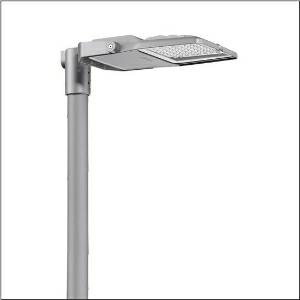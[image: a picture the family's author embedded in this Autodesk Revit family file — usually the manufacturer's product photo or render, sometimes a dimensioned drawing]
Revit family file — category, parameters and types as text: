
# Revit family: floodlight_fl_21_iq_mini___pl33t_5xa7772d2f3a_d038
name_source: partatom
category: Lighting Fixtures
units: mm (PartAtom-declared; Revit-internal decimal feet)

## family parameters
Cut with Voids When Loaded = No
Host = Face
Light Source = No
Part Type = Normal
Room Calculation Point = No
Round Connector Dimension = Use Diameter
Shared = No

## types (1)
- --- (1 x LED, 17620 lm, 143 W, 3000K)
    Apparent Load = 143 VA
    CIE Flux Codes = 26 75 99 100 100
    Color Rendering = 70
    Color Temperature = 3000K
    Default Elevation = 1800 mm
    Description = Floodlight FL 21 iQ mini, floodlight, primary light control with lens, of PMMA, primary optical cover: protective disc, of toughened safety glass, transparent, light distribution: PL33T, light emission: direct distribution, installation type: surface-mounted, lamps: LED, High Power LED, rated values: 17.620lm | 143W | 123,2lm/W (begin service life); end service life: 17.620lm | 151,6W; at 50% lumin. flux: 8.810lm | 60,6W | 145,4lm/W, colour temperature: 3000K, colour rendering: CRI > 70, light colour: 730, light setting 1 begin service life: 100% | 17.620lm | 143W | 123,2lm/W | 3.000K, light setting 1 end service life: 151,6W, further light settings possible, control: pre-setting: linear dimming characteristic, Auto-Match, Temp-Guard, Night-Set, Smart-Wire, Desk-Remote (wireless, voltage-free reading and setting of iQ features in the workshop via application-optimized NFC function/RFID function), optimised constant luminous flux control (CLO 2.0), Light-Fading, Lumen-Switch, with terminal, 6-pole, mains connection: 220..240V, AC, 50/60Hz, luminaire housing, of diecast aluminium, powder-coated, SITECO metallic grey (DB 702S), corrosivity category C5 mid according to DIN EN ISO 12944suitable for swimming poolschlorine-resistant, sealing non-destructively replaceable, please order mast flange separately, mast bracket, of steel, galvanised, powder-coated, protection rating (complete): IP66, insulation class (complete): insulation class II (safety insulation), certification: CE, ENEC, VDE, protection symbol: D, impact resistance: IK08, permissible operating ambient temperature: -40..+40°C, permissible operating ambient temperature for outdoor applications: -40..+50°C, standard: DIN EN 12944, LABS conformity tested according to VDMA 24364:2018-05, packaging unit: 1 piece

Light Distribution: PL33T
    Height = 70 mm
    Lamp = 1 x LED
    Lamp Light Flux = 17620 lm
    Lamp Power = 143 W
    Lamp count = 1
    Length = 485 mm
    Luminous efficacy = 123 lm/W
    Manufacturer = Siteco
    ModVariant = No
    Model = 5XA7772D2F3A
    Number of Poles = 1
    OnlyDefault = Yes
    Power Factor = 1
    Product Name = Floodlight FL 21 iQ mini | PL33T
    Product group = floodlight | pylon annexe
    ProductGroupID = 6201
    Protection Class = Protection class II
    Protection Degree = IP 66
    RLX_Detail_Level = 1
    RLX_Emergency_Light_Flux = 0 lm
    RLX_Emergency_Type = 0
    RLX_Emergency_Type_DB = No
    RlxData = <blob elided: 101645 chars, md5=d3f0f0db>
    Socket = socket
    Standby Power = 0 W
    System Light Flux = 17620 lm
    System Power = 143 W
    Type Comments = factory setting: luminous flux: 100 % | dim-lin: 254 | 730 mA
    Type Image = l_1007125.jpg
    URL = http://relux.com
    VarID = @adj_148427
    Voltage = 0 V
    Weight = 0.00 kg
    Width = 337 mm

## geometry (parser evidence)
native form markers: Blend x4, Sweep x13
no freeform markers — native parametric forms only
